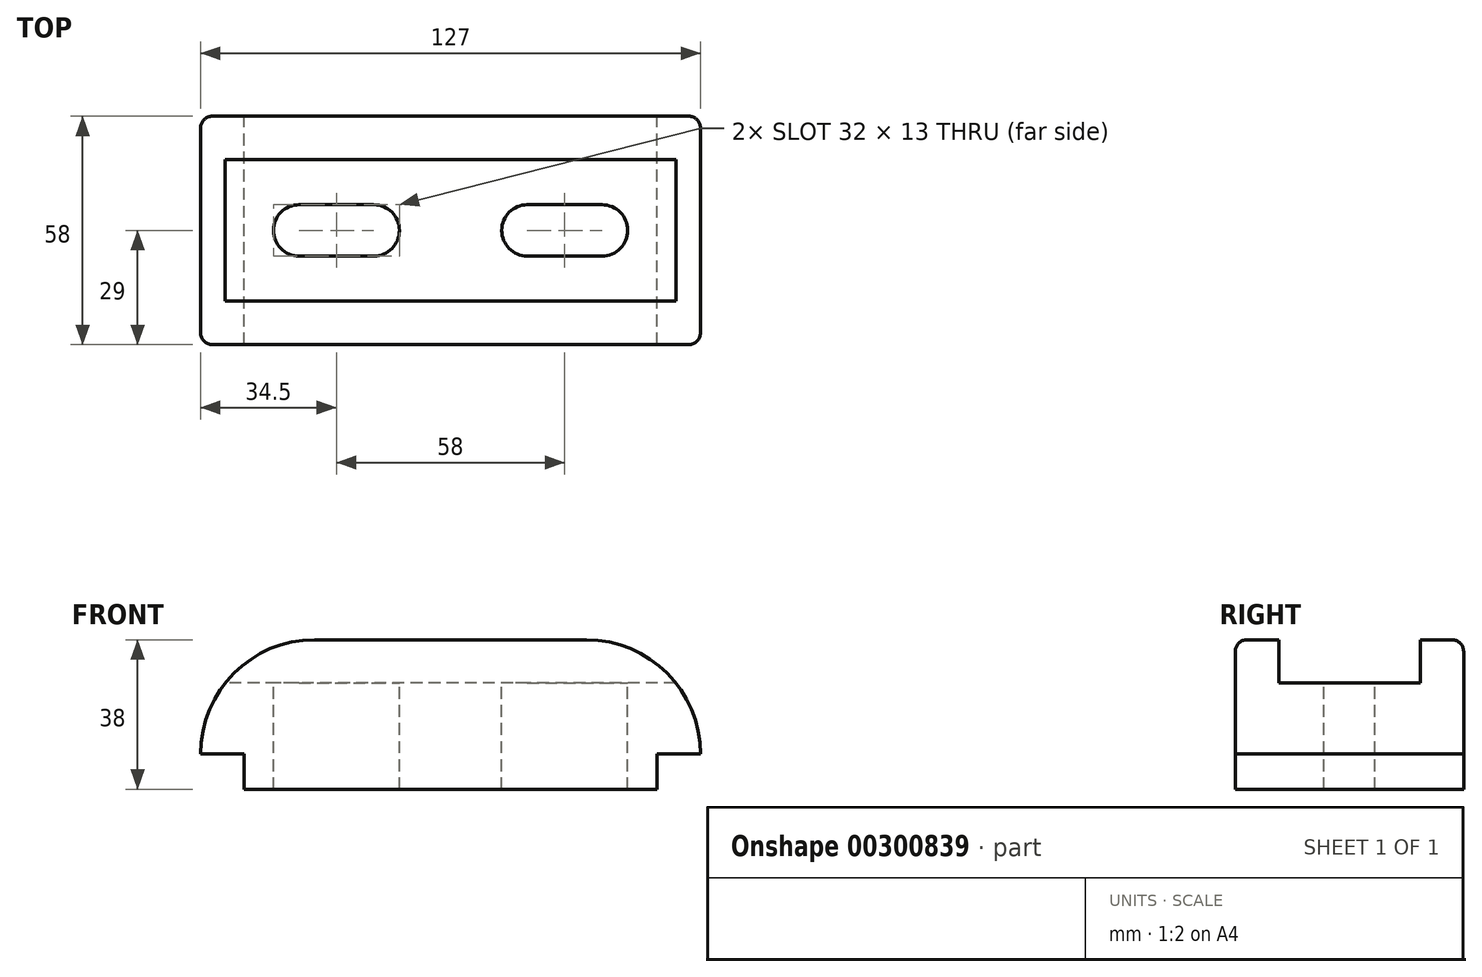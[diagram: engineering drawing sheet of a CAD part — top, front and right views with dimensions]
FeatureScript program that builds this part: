
annotation { "Feature Type Name" : "Feature", "Feature Type Description" : "" }
export const myFeature = defineFeature(function(context is Context, id is Id, definition is map)
    precondition{}
    {
        {
            var Q0;
            Q0=qCreatedBy(makeId("Front.planeOp"),FACE);
            var sketch = newSketch(context, id + "F0", { "sketchPlane" : qUnion([Q0])});
            skLineSegment(sketch, "E0", {"start": v(-63.5, 0) * mm, "end": v(-52.5, 0) * mm});
            skLineSegment(sketch, "E1", {"start": v(-52.5, 0) * mm, "end": v(-52.5, -9) * mm});
            skLineSegment(sketch, "E2", {"start": v(-52.5, -9) * mm, "end": v(52.5, -9) * mm});
            skLineSegment(sketch, "E3", {"start": v(52.5, -9) * mm, "end": v(52.5, 0) * mm});
            skLineSegment(sketch, "E4", {"start": v(52.5, 0) * mm, "end": v(63.5, 0) * mm});
            skLineSegment(sketch, "E5", {"start": v(-34.5, 29) * mm, "end": v(34.5, 29) * mm});
            skArc(sketch, "E6", {"start": v(-34.5, 29) * mm, "mid": v(-55, 20.5) * mm, "end": v(-63.5, 0) * mm});
            skArc(sketch, "E7", {"start": v(63.5, 0) * mm, "mid": v(55, 20.5) * mm, "end": v(34.5, 29) * mm});
            skSolve(sketch);
        }
        {
            var Q0;
            Q0 = qSketchRegion(id + "F0", true);
            extrude(context, id + "F1", {"entities" : qUnion([Q0]), "endBound" : BoundingType.SYMMETRIC, "depth" : 58 * mm});
        }
        {
            var Q0;
            Q0=makeQuery(id+"F1.opExtrude","SWEPT_FACE",FACE,{"disambiguationData":[OSD([sQuery(id+"F0.wireOp",EDGE,"E5")])]});
            var sketch = newSketch(context, id + "F2", { "sketchPlane" : qUnion([Q0])});
            skLineSegment(sketch, "E8.bottom", {"start": v(92.02, 18) * mm, "end": v(-92.78, 18) * mm});
            skLineSegment(sketch, "E8.top", {"start": v(92.02, -18) * mm, "end": v(-92.78, -18) * mm});
            skLineSegment(sketch, "E8.left", {"start": v(92.02, 18) * mm, "end": v(92.02, -18) * mm});
            skLineSegment(sketch, "E8.right", {"start": v(-92.78, 18) * mm, "end": v(-92.78, -18) * mm});
            skSolve(sketch);
        }
        {
            var Q0;
            Q0 = qSketchRegion(id + "F2", true);
            extrude(context, id + "F3", {"entities" : qUnion([Q0]), "operationType" : NewBodyOperationType.REMOVE, "oppositeDirection" : true, "depth" : 11 * mm});
        }
        {
            var Q0;
            Q0=makeQuery(id+"F3.boolean.opBoolean","COPY",FACE,{"derivedFrom":makeQuery(id+"F3.opExtrude","CAP_FACE",FACE,{"disambiguationData":[OSD([sQuery(id+"F2.wireOp",EDGE,"E8.bottom"),sQuery(id+"F2.wireOp",EDGE,"E8.top"),sQuery(id+"F2.wireOp",EDGE,"E8.left"),sQuery(id+"F2.wireOp",EDGE,"E8.right")])],"isStart":false})});
            var sketch = newSketch(context, id + "F4", { "sketchPlane" : qUnion([Q0])});
            skLineSegment(sketch, "E9", {"start": v(-38.5, 6.5) * mm, "end": v(-19.5, 6.5) * mm});
            skLineSegment(sketch, "E10", {"start": v(-38.5, -6.5) * mm, "end": v(-19.5, -6.5) * mm});
            skLineSegment(sketch, "E11", {"start": v(19.5, 6.5) * mm, "end": v(38.5, 6.5) * mm});
            skLineSegment(sketch, "E12", {"start": v(19.5, -6.5) * mm, "end": v(38.5, -6.5) * mm});
            skArc(sketch, "E13", {"start": v(-38.5, 6.5) * mm, "mid": v(-45, 0) * mm, "end": v(-38.5, -6.5) * mm});
            skArc(sketch, "E14", {"start": v(-19.5, -6.5) * mm, "mid": v(-13, 0) * mm, "end": v(-19.5, 6.5) * mm});
            skArc(sketch, "E15", {"start": v(19.5, 6.5) * mm, "mid": v(13, 0) * mm, "end": v(19.5, -6.5) * mm});
            skArc(sketch, "E16", {"start": v(38.5, -6.5) * mm, "mid": v(45, 0) * mm, "end": v(38.5, 6.5) * mm});
            skSolve(sketch);
        }
        {
            var Q0;
            Q0 = qSketchRegion(id + "F4", true);
            extrude(context, id + "F5", {"entities" : qUnion([Q0]), "operationType" : NewBodyOperationType.REMOVE, "endBound" : BoundingType.THROUGH_ALL, "oppositeDirection" : true, "depth" : 25 * mm});
        }
        {
            var Q0;
            Q0=makeQuery(id+"F1.opExtrude","CAP_EDGE",EDGE,{"disambiguationData":[OSD([sQuery(id+"F0.wireOp",EDGE,"E5")])],"isStart":false});
            var Q1;
            Q1=makeQuery(id+"F1.opExtrude","CAP_EDGE",EDGE,{"disambiguationData":[OSD([sQuery(id+"F0.wireOp",EDGE,"E5")])],"isStart":true});
            fillet(context, id + "F6", {"entities" : qUnion([Q0, Q1]), "radius" : 3 * mm, "tangentPropagation" : true, "allowEdgeOverflow" : false});
        }
    });
